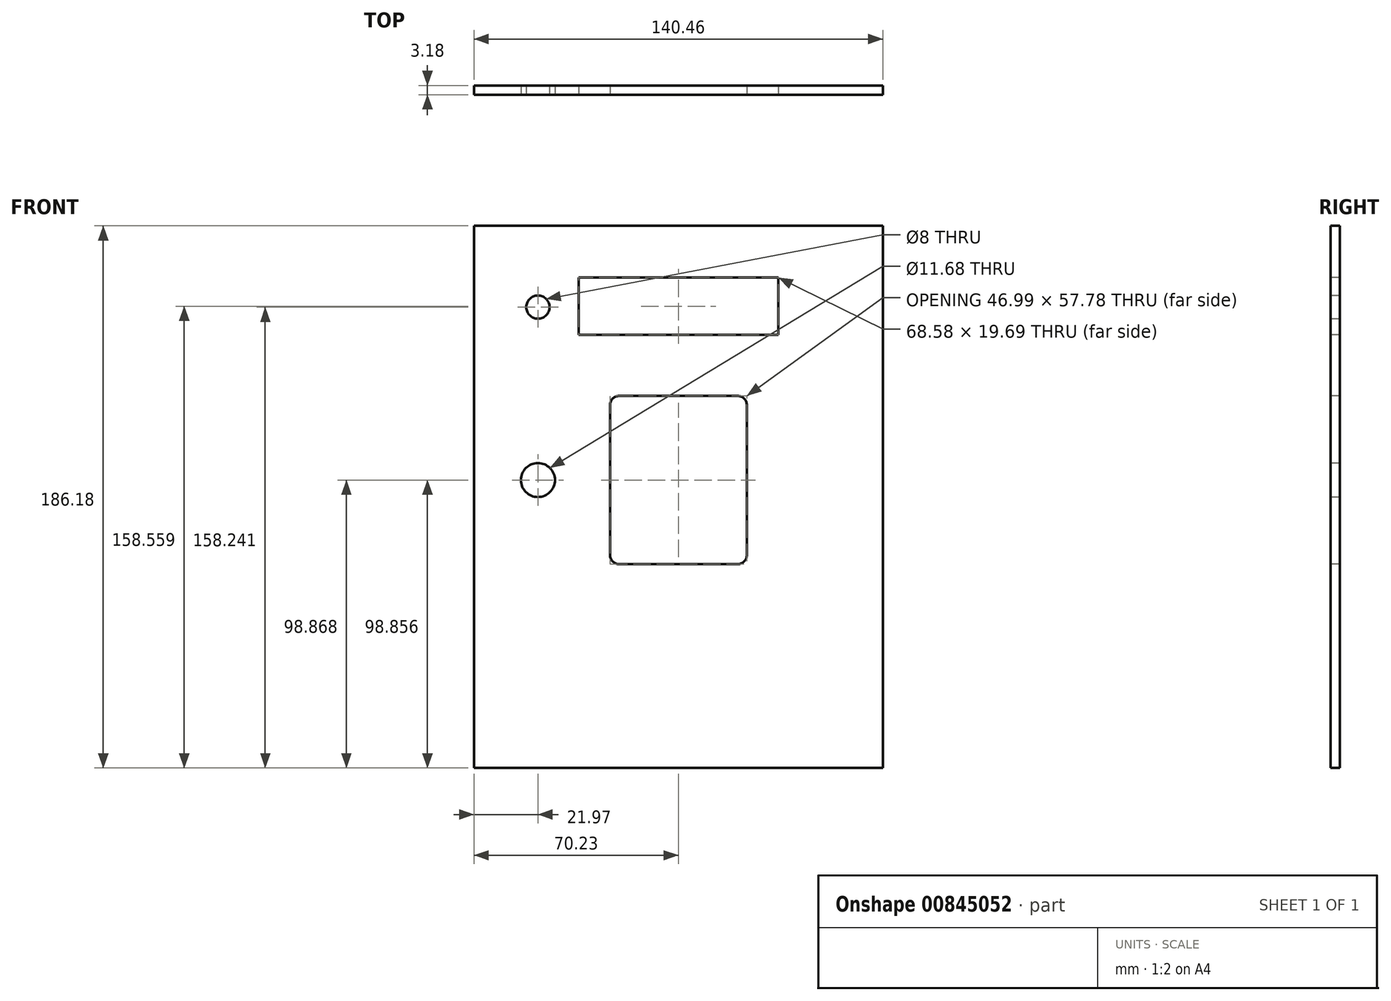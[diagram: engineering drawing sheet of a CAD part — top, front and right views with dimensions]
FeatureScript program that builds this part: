
annotation { "Feature Type Name" : "Feature", "Feature Type Description" : "" }
export const myFeature = defineFeature(function(context is Context, id is Id, definition is map)
    precondition{}
    {
        {
            var Q0;
            Q0=qCreatedBy(makeId("Front.planeOp"),FACE);
            var sketch = newSketch(context, id + "F0", { "sketchPlane" : qUnion([Q0])});
            skLineSegment(sketch, "E0.bottom", {"start": v(-70.23, 93.1) * mm, "end": v(70.23, 93.1) * mm});
            skLineSegment(sketch, "E0.top", {"start": v(-70.23, -93.1) * mm, "end": v(70.23, -93.1) * mm});
            skLineSegment(sketch, "E0.left", {"start": v(-70.23, 93.1) * mm, "end": v(-70.23, -93.1) * mm});
            skLineSegment(sketch, "E0.right", {"start": v(70.23, 93.1) * mm, "end": v(70.23, -93.1) * mm});
            skLineSegment(sketch, "E1", {"start": v(0, 0) * mm, "end": v(161.3, 0) * mm, "construction": true});
            skLineSegment(sketch, "E2", {"start": v(0, 0) * mm, "end": v(0, 116.03) * mm, "construction": true});
            skSolve(sketch);
        }
        {
            var Q0;
            Q0=makeQuery(id+"F0.imprint","IMPRINT",FACE,{"disambiguationData":[TD([[makeQuery(id+"F0.imprint","IMPRINT",EDGE,{"derivedFrom":sQuery(id+"F0.wireOp",EDGE,"E0.bottom")}),-1.0]])]});
            extrude(context, id + "F1", {"entities" : qUnion([Q0]), "depth" : 3.17 * mm, "offsetDistance" : 25.4 * mm});
        }
        {
            var Q0;
            Q0=makeQuery(id+"F1.opExtrude","CAP_FACE",FACE,{"disambiguationData":[OSD([sQuery(id+"F0.wireOp",EDGE,"E0.bottom"),sQuery(id+"F0.wireOp",EDGE,"E0.top"),sQuery(id+"F0.wireOp",EDGE,"E0.left"),sQuery(id+"F0.wireOp",EDGE,"E0.right")])],"isStart":false});
            var sketch = newSketch(context, id + "F2", { "sketchPlane" : qUnion([Q0])});
            skLineSegment(sketch, "E3", {"start": v(0, -93.1) * mm, "end": v(0, 93.1) * mm, "construction": true});
            skLineSegment(sketch, "E4.bottom", {"start": v(-34.3, 75.31) * mm, "end": v(34.3, 75.31) * mm});
            skLineSegment(sketch, "E4.top", {"start": v(-34.29, 55.63) * mm, "end": v(34.3, 55.63) * mm});
            skLineSegment(sketch, "E4.left", {"start": v(-34.3, 75.31) * mm, "end": v(-34.3, 55.63) * mm});
            skLineSegment(sketch, "E4.right", {"start": v(34.3, 75.31) * mm, "end": v(34.3, 55.63) * mm});
            skLineSegment(sketch, "E5.bottom", {"start": v(-20.32, 34.67) * mm, "end": v(20.32, 34.67) * mm});
            skLineSegment(sketch, "E5.top", {"start": v(-20.32, -23.11) * mm, "end": v(20.32, -23.11) * mm});
            skLineSegment(sketch, "E5.left", {"start": v(-23.5, 31.5) * mm, "end": v(-23.5, -19.94) * mm});
            skLineSegment(sketch, "E5.right", {"start": v(23.5, 31.5) * mm, "end": v(23.5, -19.94) * mm});
            skCircle(sketch, "E6", {"center": v(-48.26, 65.15) * mm, "radius": 4 * mm});
            skPoint(sketch, "E7.visualSharp", {"position": v(-23.5, 34.67) * mm});
            skArc(sketch, "E7.filletArc", {"start": v(-20.32, 34.67) * mm, "mid": v(-22.57, 33.74) * mm, "end": v(-23.5, 31.5) * mm});
            skPoint(sketch, "E8.visualSharp", {"position": v(23.5, 34.67) * mm});
            skArc(sketch, "E8.filletArc", {"start": v(23.5, 31.5) * mm, "mid": v(22.57, 33.74) * mm, "end": v(20.32, 34.67) * mm});
            skPoint(sketch, "E9.visualSharp", {"position": v(23.5, -23.11) * mm});
            skArc(sketch, "E9.filletArc", {"start": v(20.32, -23.11) * mm, "mid": v(22.57, -22.18) * mm, "end": v(23.5, -19.94) * mm});
            skPoint(sketch, "E10.visualSharp", {"position": v(-23.5, -23.11) * mm});
            skArc(sketch, "E10.filletArc", {"start": v(-23.5, -19.94) * mm, "mid": v(-22.57, -22.18) * mm, "end": v(-20.32, -23.11) * mm});
            skCircle(sketch, "E11", {"center": v(-48.26, 5.77) * mm, "radius": 5.84 * mm});
            skSolve(sketch);
        }
        {
            var Q0;
            Q0=makeQuery(id+"F2.imprint","IMPRINT",FACE,{"disambiguationData":[TD([[makeQuery(id+"F2.imprint","IMPRINT",EDGE,{"derivedFrom":sQuery(id+"F2.wireOp",EDGE,"E5.bottom")}),-1.0]])]});
            var Q1;
            Q1=makeQuery(id+"F2.imprint","IMPRINT",FACE,{"disambiguationData":[TD([[makeQuery(id+"F2.imprint","IMPRINT",EDGE,{"derivedFrom":sQuery(id+"F2.wireOp",EDGE,"E4.bottom")}),-1.0]])]});
            var Q2;
            Q2=makeQuery(id+"F2.imprint","IMPRINT",FACE,{"disambiguationData":[TD([[makeQuery(id+"F2.imprint","IMPRINT",EDGE,{"derivedFrom":sQuery(id+"F2.wireOp",EDGE,"E6")}),1.0]])]});
            var Q3;
            Q3=makeQuery(id+"F2.imprint","IMPRINT",FACE,{"disambiguationData":[TD([[makeQuery(id+"F2.imprint","IMPRINT",EDGE,{"derivedFrom":sQuery(id+"F2.wireOp",EDGE,"E11")}),1.0]])]});
            extrude(context, id + "F3", {"entities" : qUnion([Q0, Q1, Q2, Q3]), "operationType" : NewBodyOperationType.REMOVE, "endBound" : BoundingType.THROUGH_ALL, "oppositeDirection" : true, "depth" : 25.4 * mm, "offsetDistance" : 25.4 * mm});
        }
    });
